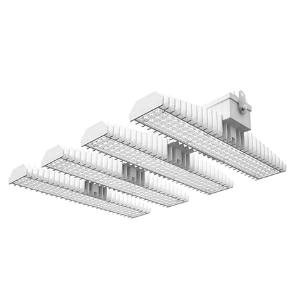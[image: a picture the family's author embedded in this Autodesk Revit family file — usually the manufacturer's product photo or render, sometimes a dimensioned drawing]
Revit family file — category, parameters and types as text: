
# Revit family: 3f_filippi_-_3f_lem_ampio_3f_filippi_-_58902_a0811_-_3f_lem_4_led_200_dali_cr_ampio___vt_bfae
name_source: partatom
category: Lighting Fixtures
units: mm (PartAtom-declared; Revit-internal decimal feet)

## family parameters
Cut with Voids When Loaded = No
Host = Face
Light Source = No
Part Type = Normal
Room Calculation Point = No
Round Connector Dimension = Use Diameter
Shared = No

## types (1)
- 3F Filippi - 3F LEM Ampio (1 x LED, 31641 lm, 218 W, 4000 K)
    Apparent Load = 218 VA
    Approval mark = CE
    CIE Flux Codes = 60 92 99 100 100
    Color Rendering = 80
    Color Temperature = 4000 K
    Control Gear = Electronic transformer
    Default Elevation = 1800 mm
    Description = Industrial luminaire with high light output and high luminous efficiency designed with the most innovative technologies for environments with temperature up to 55°C.

ILLUMINOTECHNICAL
Luminous efficiency 100% (DLOR 99%, ULOR 1%).
Initial luminous flux of the luminaire 31641 lm.
Direct symmetric wide distribution: the illuminated area has a rectangular shape.
Installation Interdistance Transv.D = 1.58 x hu - Long.D = 1.45 x hu.
Tabular UGR (CIE 117 - 4H-8H; S=0.25H; 70/50/20): RUG 22.9 - 23.9.
Beam angle: 93° - 99°.
Luminous efficacy 145 lm/W.
Lifetime (L93/B10): 30000 h. (tq+25°C)
Lifetime (L90/B10): 50000 h. (tq+25°C)
Lifetime (L85/B10): 80000 h. (tq+25°C)
Lifetime (L80/B10): 100000 h. (tq+25°C)
Lifetime (L85/B10): 50000 h. (tq+55°C)
Sudden decreased luminous flux after 50000 hours: 0% (C0).
Photobiological safety in compliance with IEC/TR 62778: RG0 risk exempt, (IEC 62471).
In compliance with IEC/EN 62722-2-1 - IEC/EN 62717 standards.

SOURCE
4 Mid-Power linear LED modules 50W/840.
Energy efficiency class (UE 2019/2020 - UE 2019/2015): C.
CIE 13.3 Colour rendering index: CRI >80 (R9 <50%).
IES TM-30 Fidelity Index: Rf = 84 Rg = 95.
CCT nominal colour temperature 4000 K.
Colour initial tolerance (MacAdam): SDCM 3.

MECHANICAL
Passive modular heatsinks in die-casted aluminium, painted in white colour.
To optimize the thermal management of the LED module, the heatsinks are oversized and provided with self-cleaning of cooling fins.
Wiring body in aluminium and galvanised steel anchored solidly to the sinks and thermally separated.
3F Lens lenses with high luminous efficiency, transparent methacrylate (PMMA), fixed to the LED modules.
Fixing brackets in stainless steel.
Luminaire with limited surface temperature. - D - (EN 60598-2-24)
Dimensions: 757x542 mm, height 133 mm. Weight 19.433 kg.
IP65 protection degree.
Mechanical strength to impacts IK06 (1 joule).
Glow-wire test resistance 650°C.

ELECTRICAL
Halogen Free DALI-2 DATI (Parts 251, 252, 253), PUSH-DIM, electronic wiring 230V-50/60Hz, power factor 0.97 at full load, THD <25%, constant output current, class I, 2 driver, 2 DALI addresses.
Power of the luminaire 218 W.
ENEC - CE.
Flicker: <4%.
Luminaire compliant with EN 60598-2-22 for power supply from a centralised emergency system CPSS (Central Power Supply System), not incorporated in the luminaire - high risk areas excluded. The default power and flux are 100% in AC and 15% in DC.
Ambient temperature from -30°C to +55°C.
Temperature class T6 max 85°C.
Quick connection via M25 5P connector with 9-13 mm tightening range.
Power unit positioned on a separate compartment by the LED module to ensure optimum temperatures of cabling components, to be inspectable and maintainable.
Relative humidity UR: <85%.

INSTALLATION
Ceiling / Suspended / Wall.
All accessories dedicated to this product are available on the Catalog and on our website www.3F-Filippi.com.

ACCESSORIES
A0811 - VT transparent glass, tempered, not flammable, with sealing gasket.
One required for each light module. The pack contains 10 pieces.

APPLICATIONS
In commercial environments, exhibition and industrial areas, stores, open areas.
Applications with high ambient temperature up to 55°C.
Environments in which it is necessary a total protection against falling fragments (eg environments with foodstuffs or machines with moving parts or with extreme temperature changes), use luminaires with polycarbonate lenses.

LIGHT MANAGEMENT
Recommended minimum setting: 10%.
The luminaire, equipped with (DALI-2 DATI) driver, can be controlled manually with 3F Easy Dim technology or automatically/manually with wired or wireless DALI/D2D control systems.
The D2D driver guarantees interoperability with other devices with the same certification by making the following information available:
Device Data (Part 251), Energy Report (Part 252), Diagnosis & Maintenance (Part 253).
In electrical systems without a regulation system (manual or automatic) and DALI bus, a suitable jumper must be made on the DA-DA terminals of the appliance.

WARNING
Fixture not suitable for cold stores with an ambient temperature <0°C and/or relative humidity >85%.
Luminaire designed for disposal/recycling at end-of-life.
Replaceable (LED only) light source by a professional. Replaceable control gear by a professional.
    Height = 133 mm  [stored 0.436352 ft]
    Lamp = 1 x LED
    Lamp Light Flux = 31641 lm
    Lamp Power = 218 W
    Lamp count = 1
    Length = 757 mm
    Lifetime = 50000 h
    Luminous efficacy = 145 lm/W
    Manufacturer = 3F Filippi
    ModVariant = No
    Model = 3F Filippi - 58902+A0811 - 3F LEM 4 LED 200 DALI CR AMPIO + VT
    Mounting Place = Ceiling
    Mounting Type = Pendant
    Number of Poles = 1
    OnlyDefault = Yes
    Power Factor = 1
    Product Name = 3F Filippi - 3F LEM Ampio
    Product group = pendant luminaire
    ProductGroupID = 9
    Protection Class = Protection class I
    Protection Degree = IP 65
    RLX_Detail_Level = 1
    RLX_Emergency_Light_Flux = 0 lm
    RLX_Emergency_Type = 0
    RLX_Emergency_Type_DB = No
    RlxData = <blob elided: 120421 chars, md5=fa97e049>
    Socket = socket
    Standby Power = 0 W
    System Light Flux = 31641 lm
    System Power = 218 W
    Type Comments = Product without accessories
    Type Image = 3f_filippi_-_lem_4__a0811.jpg
    URL = http://relux.com
    VarID = ---
    Voltage = 0 V
    Weight = 0.00 kg
    Width = 542 mm

note: [stored X ft] marks values corroborated as IEEE doubles in the binary element streams (Revit-internal decimal feet)

## geometry (parser evidence)
native form markers: Blend x4, Sweep x13
no freeform markers — native parametric forms only
